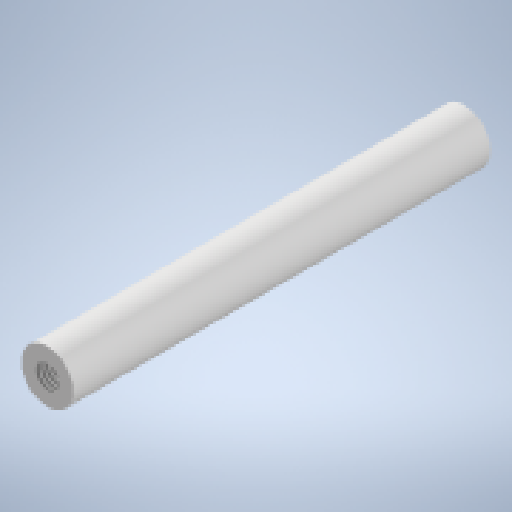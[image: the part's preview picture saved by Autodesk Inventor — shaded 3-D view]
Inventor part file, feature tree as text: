
AUTODESK INVENTOR PART (.ipt)
format: ipt  version: 2023 (Build 270158000, 158)  size: 152,576 bytes
history: native  units: mm
features: extrude x3, sketch x3, thread x2
ambient origin geometry x8: Origin, YZ Plane, XZ Plane, XY Plane, X Axis, Y Axis, Z Axis, Center Point
bodies: Solid1 (feature_tree)
feature tree (8):
  extrude  "Extrusion1"  Depth=40.0mm TaperAngle=0.0deg
  extrude  "Extrusion2"  Depth=20.0mm TaperAngle=0.0deg
  extrude  "Extrusion3"  Depth=16.0mm TaperAngle=0.0deg
  thread  "Thread1"  [1 undecoded]
  thread  "Thread2"  [1 undecoded]
  sketch  "Sketch1"  dims[d0=5.0mm d1=40.0mm d2=0.0mm]
  sketch  "Sketch2"  dims[d3=2.2mm d4=20.0mm d5=0.0mm]
  sketch  "Sketch3"  dims[d6=20.0mm d7=0.0mm d8=16.0mm d9=0.0mm d10=16.0mm d11=0.0mm]
note: 2 required parameter values undecoded (feature->parameter linkage not recoverable at this tier; creation-order binding heuristic only, values carry confidence <= 0.55)
